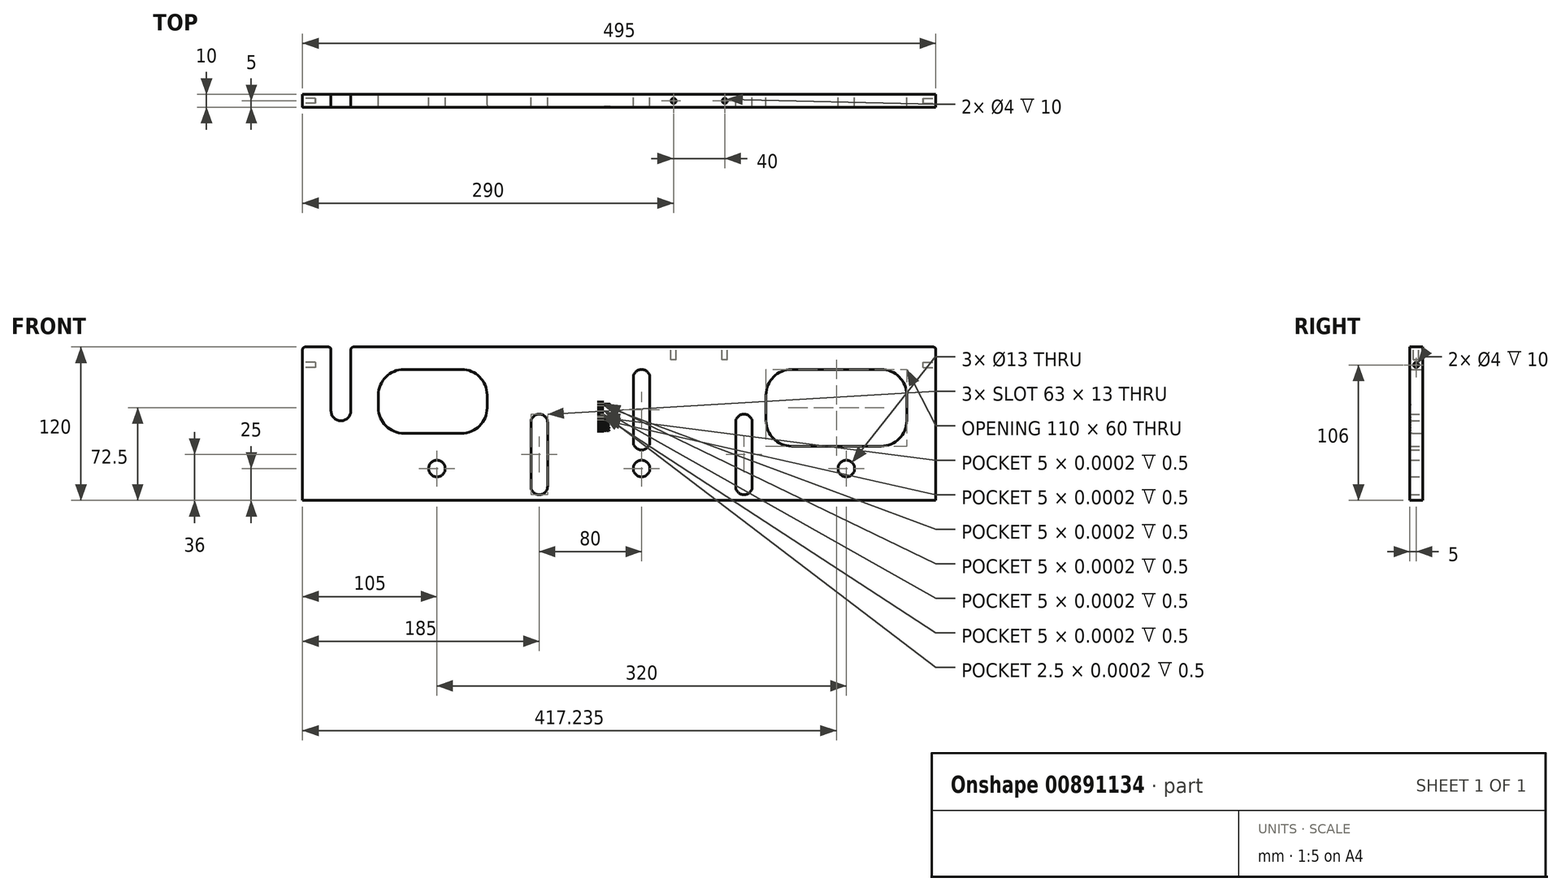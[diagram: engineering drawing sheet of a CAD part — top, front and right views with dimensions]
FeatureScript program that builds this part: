
annotation { "Feature Type Name" : "Feature", "Feature Type Description" : "" }
export const myFeature = defineFeature(function(context is Context, id is Id, definition is map)
    precondition{}
    {
        {
            var Q0;
            Q0=qCreatedBy(makeId("Front.planeOp"),FACE);
            var sketch = newSketch(context, id + "F0", { "sketchPlane" : qUnion([Q0])});
            skLineSegment(sketch, "E0.bottom", {"start": v(-247.5, -60) * mm, "end": v(247.5, -60) * mm});
            skLineSegment(sketch, "E0.top", {"start": v(-247.5, 60) * mm, "end": v(-225.25, 60) * mm});
            skLineSegment(sketch, "E0.left", {"start": v(-247.5, -60) * mm, "end": v(-247.5, 60) * mm});
            skLineSegment(sketch, "E0.right", {"start": v(247.5, -60) * mm, "end": v(247.5, 60) * mm});
            skPoint(sketch, "E0.middle", {"position": v(0, 0) * mm});
            skArc(sketch, "E1", {"start": v(-225.25, 10) * mm, "mid": v(-217.5, 2.25) * mm, "end": v(-209.75, 10) * mm});
            skLineSegment(sketch, "E2", {"start": v(-225.25, 10) * mm, "end": v(-225.25, 60) * mm});
            skLineSegment(sketch, "E3", {"start": v(-209.75, 10) * mm, "end": v(-209.75, 60) * mm});
            skLineSegment(sketch, "E4.trimOffspring", {"start": v(-209.75, 60) * mm, "end": v(247.5, 60) * mm});
            skArc(sketch, "E5", {"start": v(-69, -49) * mm, "mid": v(-62.5, -55.5) * mm, "end": v(-56, -49) * mm});
            skLineSegment(sketch, "E6", {"start": v(17.5, -50) * mm, "end": v(17.5, -10) * mm, "construction": true});
            skLineSegment(sketch, "E7", {"start": v(-62.5, -49) * mm, "end": v(-62.5, 9.6) * mm, "construction": true});
            skLineSegment(sketch, "E8", {"start": v(97.5, -8.77) * mm, "end": v(97.5, -64.84) * mm, "construction": true});
            skArc(sketch, "E9", {"start": v(11, -14) * mm, "mid": v(17.5, -20.5) * mm, "end": v(24, -14) * mm});
            skArc(sketch, "E10", {"start": v(24, 36) * mm, "mid": v(17.5, 42.5) * mm, "end": v(11, 36) * mm});
            skLineSegment(sketch, "E11", {"start": v(11, -14) * mm, "end": v(11, 36) * mm});
            skLineSegment(sketch, "E12.MirrorCS", {"start": v(24, -14) * mm, "end": v(24, 36) * mm});
            skCircle(sketch, "E13", {"center": v(-142.5, -35) * mm, "radius": 6.5 * mm});
            skCircle(sketch, "E14.MirrorC", {"center": v(17.5, -35) * mm, "radius": 6.5 * mm});
            skCircle(sketch, "E15.MirrorC", {"center": v(177.5, -35) * mm, "radius": 6.5 * mm});
            skLineSegment(sketch, "E16", {"start": v(-56, -49) * mm, "end": v(-56, 1) * mm});
            skLineSegment(sketch, "E17.MirrorCS", {"start": v(-69, -49) * mm, "end": v(-69, 1) * mm});
            skArc(sketch, "E18", {"start": v(-56, 1) * mm, "mid": v(-62.5, 7.5) * mm, "end": v(-69, 1) * mm});
            skLineSegment(sketch, "E19.MirrorCS", {"start": v(91, -49) * mm, "end": v(91, 1) * mm});
            skLineSegment(sketch, "E20.MirrorCS", {"start": v(104, -49) * mm, "end": v(104, 1) * mm});
            skArc(sketch, "E21.MirrorCS", {"start": v(91, 1) * mm, "mid": v(97.5, 7.5) * mm, "end": v(104, 1) * mm});
            skPoint(sketch, "E22.orphan", {"position": v(104, -49) * mm});
            skPoint(sketch, "E23.MirrorC.center.orphan", {"position": v(97.5, -49) * mm});
            skPoint(sketch, "E24.MirrorCS.end.orphan", {"position": v(91, -49) * mm});
            skArc(sketch, "E25.MirrorCS", {"start": v(104, -49) * mm, "mid": v(97.5, -55.5) * mm, "end": v(91, -49) * mm});
            skLineSegment(sketch, "E26.bottom", {"start": v(-168.22, 42.5) * mm, "end": v(-123.22, 42.5) * mm});
            skLineSegment(sketch, "E26.top", {"start": v(-168.22, -7.5) * mm, "end": v(-123.22, -7.5) * mm});
            skLineSegment(sketch, "E26.left", {"start": v(-188.22, 22.5) * mm, "end": v(-188.22, 12.5) * mm});
            skLineSegment(sketch, "E26.right", {"start": v(-103.22, 22.5) * mm, "end": v(-103.22, 12.5) * mm});
            skLineSegment(sketch, "E27.bottom", {"start": v(134.73, 42.5) * mm, "end": v(204.73, 42.5) * mm});
            skLineSegment(sketch, "E27.top", {"start": v(134.73, -17.5) * mm, "end": v(204.73, -17.5) * mm});
            skLineSegment(sketch, "E27.left", {"start": v(114.73, 22.5) * mm, "end": v(114.73, 2.5) * mm});
            skLineSegment(sketch, "E27.right", {"start": v(224.73, 22.5) * mm, "end": v(224.73, 2.5) * mm});
            skPoint(sketch, "E28.visualSharp", {"position": v(-188.22, 42.5) * mm});
            skArc(sketch, "E28.filletArc", {"start": v(-168.22, 42.5) * mm, "mid": v(-182.36, 36.64) * mm, "end": v(-188.22, 22.5) * mm});
            skPoint(sketch, "E29.visualSharp", {"position": v(-103.22, 42.5) * mm});
            skArc(sketch, "E29.filletArc", {"start": v(-103.22, 22.5) * mm, "mid": v(-109.08, 36.64) * mm, "end": v(-123.22, 42.5) * mm});
            skPoint(sketch, "E30.visualSharp", {"position": v(-188.22, -7.5) * mm});
            skArc(sketch, "E30.filletArc", {"start": v(-188.22, 12.5) * mm, "mid": v(-182.36, -1.64) * mm, "end": v(-168.22, -7.5) * mm});
            skPoint(sketch, "E31.visualSharp", {"position": v(-103.22, -7.5) * mm});
            skArc(sketch, "E31.filletArc", {"start": v(-123.22, -7.5) * mm, "mid": v(-109.08, -1.64) * mm, "end": v(-103.22, 12.5) * mm});
            skPoint(sketch, "E32.visualSharp", {"position": v(114.73, 42.5) * mm});
            skArc(sketch, "E32.filletArc", {"start": v(134.73, 42.5) * mm, "mid": v(120.6, 36.64) * mm, "end": v(114.73, 22.5) * mm});
            skPoint(sketch, "E33.visualSharp", {"position": v(224.73, -17.5) * mm});
            skArc(sketch, "E33.filletArc", {"start": v(204.73, -17.5) * mm, "mid": v(218.88, -11.64) * mm, "end": v(224.73, 2.5) * mm});
            skPoint(sketch, "E34.visualSharp", {"position": v(224.73, 42.5) * mm});
            skArc(sketch, "E34.filletArc", {"start": v(224.73, 22.5) * mm, "mid": v(218.88, 36.64) * mm, "end": v(204.73, 42.5) * mm});
            skPoint(sketch, "E35.visualSharp", {"position": v(114.73, -17.5) * mm});
            skArc(sketch, "E35.filletArc", {"start": v(114.73, 2.5) * mm, "mid": v(120.6, -11.64) * mm, "end": v(134.73, -17.5) * mm});
            skSolve(sketch);
        }
        {
            var Q0;
            Q0=qSketchRegion(id+"F0",true);
            extrude(context, id + "F1", {"entities" : qUnion([Q0]), "endBound" : BoundingType.SYMMETRIC, "depth" : 10 * mm, "offsetDistance" : 25 * mm});
        }
        {
            var Q0;
            Q0=makeQuery(id+"F1.opExtrude","SWEPT_FACE",FACE,{"disambiguationData":[OSD([sQuery(id+"F0.wireOp",EDGE,"E4.trimOffspring")])]});
            var sketch = newSketch(context, id + "F2", { "sketchPlane" : qUnion([Q0])});
            skLineSegment(sketch, "E36", {"start": v(62.5, 81.53) * mm, "end": v(62.5, -22.42) * mm, "construction": true});
            skCircle(sketch, "E37", {"center": v(42.5, 0) * mm, "radius": 2 * mm});
            skCircle(sketch, "E38.MirrorC", {"center": v(82.5, 0) * mm, "radius": 2 * mm});
            skSolve(sketch);
        }
        {
            var Q0;
            Q0=qSketchRegion(id+"F2",true);
            extrude(context, id + "F3", {"entities" : qUnion([Q0]), "operationType" : NewBodyOperationType.REMOVE, "oppositeDirection" : true, "depth" : 10 * mm, "offsetDistance" : 25 * mm});
        }
        {
            var Q0;
            Q0=makeQuery(id+"F1.opExtrude","SWEPT_EDGE",EDGE,{"disambiguationData":[OSD([sQuery(id+"F0.wireOp",EDGE,"E0.top"),sQuery(id+"F0.wireOp",EDGE,"E2")])]});
            var Q1;
            Q1=makeQuery(id+"F1.opExtrude","SWEPT_EDGE",EDGE,{"disambiguationData":[OSD([sQuery(id+"F0.wireOp",EDGE,"E0.top"),sQuery(id+"F0.wireOp",EDGE,"E0.left")])]});
            var Q2;
            Q2=makeQuery(id+"F1.opExtrude","SWEPT_EDGE",EDGE,{"disambiguationData":[OSD([sQuery(id+"F0.wireOp",EDGE,"E3"),sQuery(id+"F0.wireOp",EDGE,"E4.trimOffspring")])]});
            var Q3;
            Q3=makeQuery(id+"F1.opExtrude","SWEPT_EDGE",EDGE,{"disambiguationData":[OSD([sQuery(id+"F0.wireOp",EDGE,"E0.right"),sQuery(id+"F0.wireOp",EDGE,"E4.trimOffspring")])]});
            fillet(context, id + "F4", {"entities" : qUnion([Q0, Q1, Q2, Q3]), "radius" : 2 * mm, "tangentPropagation" : true, "allowEdgeOverflow" : false});
        }
        {
            var Q0;
            Q0=makeQuery(id+"F1.opExtrude","SWEPT_FACE",FACE,{"disambiguationData":[OSD([sQuery(id+"F0.wireOp",EDGE,"E0.left")])]});
            var sketch = newSketch(context, id + "F5", { "sketchPlane" : qUnion([Q0])});
            skCircle(sketch, "E39", {"center": v(0, 46) * mm, "radius": 2 * mm});
            skSolve(sketch);
        }
        {
            var Q0;
            Q0=makeQuery(id+"F1.opExtrude","SWEPT_FACE",FACE,{"disambiguationData":[OSD([sQuery(id+"F0.wireOp",EDGE,"E0.right")])]});
            var sketch = newSketch(context, id + "F6", { "sketchPlane" : qUnion([Q0])});
            skCircle(sketch, "E40", {"center": v(0, 46) * mm, "radius": 2 * mm});
            skSolve(sketch);
        }
        {
            var Q0;
            Q0 = qSketchRegion(id + "F5", true);
            extrude(context, id + "F7", {"entities" : qUnion([Q0]), "operationType" : NewBodyOperationType.REMOVE, "oppositeDirection" : true, "depth" : 10 * mm, "offsetDistance" : 25 * mm});
        }
        {
            var Q0;
            Q0 = qSketchRegion(id + "F6", true);
            extrude(context, id + "F8", {"entities" : qUnion([Q0]), "operationType" : NewBodyOperationType.REMOVE, "oppositeDirection" : true, "depth" : 10 * mm, "offsetDistance" : 25 * mm});
        }
        {
            var Q0;
            Q0=makeQuery(id+"F1.opExtrude","CAP_FACE",FACE,{"disambiguationData":[OSD([sQuery(id+"F0.wireOp",EDGE,"E0.bottom"),sQuery(id+"F0.wireOp",EDGE,"E0.top"),sQuery(id+"F0.wireOp",EDGE,"E0.left"),sQuery(id+"F0.wireOp",EDGE,"E0.right"),sQuery(id+"F0.wireOp",EDGE,"E1"),sQuery(id+"F0.wireOp",EDGE,"E2"),sQuery(id+"F0.wireOp",EDGE,"E3"),sQuery(id+"F0.wireOp",EDGE,"E4.trimOffspring"),sQuery(id+"F0.wireOp",EDGE,"E5"),sQuery(id+"F0.wireOp",EDGE,"E9"),sQuery(id+"F0.wireOp",EDGE,"E10"),sQuery(id+"F0.wireOp",EDGE,"E11"),sQuery(id+"F0.wireOp",EDGE,"E12.MirrorCS"),sQuery(id+"F0.wireOp",EDGE,"E13"),sQuery(id+"F0.wireOp",EDGE,"E14.MirrorC"),sQuery(id+"F0.wireOp",EDGE,"E15.MirrorC"),sQuery(id+"F0.wireOp",EDGE,"E16"),sQuery(id+"F0.wireOp",EDGE,"E17.MirrorCS"),sQuery(id+"F0.wireOp",EDGE,"E18"),sQuery(id+"F0.wireOp",EDGE,"E19.MirrorCS"),sQuery(id+"F0.wireOp",EDGE,"E20.MirrorCS"),sQuery(id+"F0.wireOp",EDGE,"E21.MirrorCS"),sQuery(id+"F0.wireOp",EDGE,"E25.MirrorCS")])],"isStart":false});
            var sketch = newSketch(context, id + "F9", { "sketchPlane" : qUnion([Q0])});
            skLineSegment(sketch, "E41", {"start": v(17.5, -14) * mm, "end": v(-16.83, -14) * mm, "construction": true});
            skLineSegment(sketch, "E42.bottom", {"start": v(-17, -6) * mm, "end": v(-12, -6) * mm});
            skLineSegment(sketch, "E42.top", {"start": v(-17, -6) * mm, "end": v(-12, -6) * mm});
            skLineSegment(sketch, "E42.left", {"start": v(-17, -6) * mm, "end": v(-17, -6) * mm});
            skLineSegment(sketch, "E42.right", {"start": v(-12, -6) * mm, "end": v(-12, -6) * mm});
            skPoint(sketch, "E42.middle", {"position": v(-14.5, -6) * mm});
            skPoint(sketch, "E43.orphan", {"position": v(-17, -6) * mm});
            skLineSegment(sketch, "E44", {"start": v(-34.94, -5.75) * mm, "end": v(-8.14, -5.75) * mm, "construction": true});
            skLineSegment(sketch, "E45.MirrorCS", {"start": v(-14.5, -5.5) * mm, "end": v(-12, -5.5) * mm});
            skLineSegment(sketch, "E46.MirrorCS", {"start": v(-12, -5.5) * mm, "end": v(-12, -5.5) * mm});
            skLineSegment(sketch, "E47", {"start": v(-17, -5.3) * mm, "end": v(-16.3, -5.3) * mm, "construction": true});
            skLineSegment(sketch, "E48", {"start": v(-17, -5.5) * mm, "end": v(-16.28, -5.5) * mm, "construction": true});
            skLineSegment(sketch, "E49", {"start": v(-17, -6) * mm, "end": v(-16.85, -6) * mm, "construction": true});
            skLineSegment(sketch, "E50", {"start": v(-14.5, -5.5) * mm, "end": v(-14.5, -5.5) * mm});
            skLineSegment(sketch, "E51.MirrorCS", {"start": v(-17, -5) * mm, "end": v(-12, -5) * mm});
            skLineSegment(sketch, "E52.MirrorCS", {"start": v(-17, -5) * mm, "end": v(-17, -5) * mm});
            skLineSegment(sketch, "E53.MirrorCS", {"start": v(-17, -5) * mm, "end": v(-16.85, -5) * mm, "construction": true});
            skLineSegment(sketch, "E54.MirrorCS", {"start": v(-12, -5) * mm, "end": v(-12, -5) * mm});
            skLineSegment(sketch, "E55.MirrorCS", {"start": v(-17, -4) * mm, "end": v(-12, -4) * mm});
            skLineSegment(sketch, "E56.MirrorCS", {"start": v(-17, -4) * mm, "end": v(-17, -4) * mm});
            skLineSegment(sketch, "E57.MirrorCS", {"start": v(-12, -4) * mm, "end": v(-12, -4) * mm});
            skLineSegment(sketch, "E58.MirrorCS", {"start": v(-17, -4) * mm, "end": v(-16.85, -4) * mm, "construction": true});
            skLineSegment(sketch, "E59.MirrorCS", {"start": v(-14.5, -4.5) * mm, "end": v(-12, -4.5) * mm});
            skLineSegment(sketch, "E60.MirrorCS", {"start": v(-14.5, -4.5) * mm, "end": v(-14.5, -4.5) * mm});
            skLineSegment(sketch, "E61.MirrorCS", {"start": v(-12, -4.5) * mm, "end": v(-12, -4.5) * mm});
            skLineSegment(sketch, "E62.MirrorCS", {"start": v(-14.5, -3.5) * mm, "end": v(-12, -3.5) * mm});
            skLineSegment(sketch, "E63.MirrorCS", {"start": v(-14.5, -3.5) * mm, "end": v(-14.5, -3.5) * mm});
            skLineSegment(sketch, "E64.MirrorCS", {"start": v(-12, -3.5) * mm, "end": v(-12, -3.5) * mm});
            skLineSegment(sketch, "E65", {"start": v(-14.58, -3.5) * mm, "end": v(-14.5, -3.5) * mm, "construction": true});
            skLineSegment(sketch, "E66.MirrorCS", {"start": v(-12, -2) * mm, "end": v(-12, -2) * mm});
            skLineSegment(sketch, "E67.MirrorCS", {"start": v(-17, -2) * mm, "end": v(-16.85, -2) * mm, "construction": true});
            skLineSegment(sketch, "E68.MirrorCS", {"start": v(-17, -1) * mm, "end": v(-16.85, -1) * mm, "construction": true});
            skLineSegment(sketch, "E69.MirrorCS", {"start": v(-17, -1) * mm, "end": v(-17, -1) * mm});
            skLineSegment(sketch, "E70.MirrorCS", {"start": v(-17, -2) * mm, "end": v(-17, -2) * mm});
            skLineSegment(sketch, "E71.MirrorCS", {"start": v(-17, -3) * mm, "end": v(-16.85, -3) * mm, "construction": true});
            skLineSegment(sketch, "E72.MirrorCS", {"start": v(-12, -1.5) * mm, "end": v(-12, -1.5) * mm});
            skLineSegment(sketch, "E73.MirrorCS", {"start": v(-12, -1) * mm, "end": v(-12, -1) * mm});
            skLineSegment(sketch, "E74.MirrorCS", {"start": v(-12, -2.5) * mm, "end": v(-12, -2.5) * mm});
            skLineSegment(sketch, "E75.MirrorCS", {"start": v(-12, -3) * mm, "end": v(-12, -3) * mm});
            skLineSegment(sketch, "E76.MirrorCS", {"start": v(-14.5, -1.5) * mm, "end": v(-14.5, -1.5) * mm});
            skLineSegment(sketch, "E77.MirrorCS", {"start": v(-17, -3) * mm, "end": v(-17, -3) * mm});
            skLineSegment(sketch, "E78.MirrorCS", {"start": v(-14.5, -2.5) * mm, "end": v(-14.5, -2.5) * mm});
            skLineSegment(sketch, "E79.MirrorCS", {"start": v(-14.5, -1.5) * mm, "end": v(-12, -1.5) * mm});
            skLineSegment(sketch, "E80.MirrorCS", {"start": v(-17, -2) * mm, "end": v(-12, -2) * mm});
            skLineSegment(sketch, "E81.MirrorCS", {"start": v(-17, -1.5) * mm, "end": v(-16.28, -1.5) * mm, "construction": true});
            skLineSegment(sketch, "E82.MirrorCS", {"start": v(-17, -1.7) * mm, "end": v(-16.3, -1.7) * mm, "construction": true});
            skLineSegment(sketch, "E83.MirrorCS", {"start": v(-17, -1) * mm, "end": v(-12, -1) * mm});
            skLineSegment(sketch, "E84.MirrorCS", {"start": v(-14.5, -2.5) * mm, "end": v(-12, -2.5) * mm});
            skLineSegment(sketch, "E85.MirrorCS", {"start": v(-17, -3) * mm, "end": v(-12, -3) * mm});
            skPoint(sketch, "E86.MirrorP", {"position": v(-17, -1) * mm});
            skPoint(sketch, "E87.MirrorP", {"position": v(-14.5, -1) * mm});
            skLineSegment(sketch, "E88.MirrorCS", {"start": v(-14.5, -0.5) * mm, "end": v(-14.5, -0.5) * mm});
            skLineSegment(sketch, "E89.MirrorCS", {"start": v(-14.5, -0.5) * mm, "end": v(-12, -0.5) * mm});
            skLineSegment(sketch, "E90.MirrorCS", {"start": v(-12, -0.5) * mm, "end": v(-12, -0.5) * mm});
            skLineSegment(sketch, "E91", {"start": v(-14.72, -0.5) * mm, "end": v(-14.5, -0.5) * mm, "construction": true});
            skLineSegment(sketch, "E92", {"start": v(-32.7, -1.5) * mm, "end": v(-14.5, -1.5) * mm, "construction": true});
            skLineSegment(sketch, "E93.MirrorCS", {"start": v(-12, 1.5) * mm, "end": v(-12, 1.5) * mm});
            skLineSegment(sketch, "E94.MirrorCS", {"start": v(-17, 0) * mm, "end": v(-16.85, 0) * mm, "construction": true});
            skLineSegment(sketch, "E95.MirrorCS", {"start": v(-17, 0) * mm, "end": v(-17, 0) * mm});
            skLineSegment(sketch, "E96.MirrorCS", {"start": v(-17, 4) * mm, "end": v(-17, 4) * mm});
            skLineSegment(sketch, "E97.MirrorCS", {"start": v(-12, 4) * mm, "end": v(-12, 4) * mm});
            skLineSegment(sketch, "E98.MirrorCS", {"start": v(-17, 4) * mm, "end": v(-16.85, 4) * mm, "construction": true});
            skLineSegment(sketch, "E99.MirrorCS", {"start": v(-14.5, 1.5) * mm, "end": v(-14.5, 1.5) * mm});
            skLineSegment(sketch, "E100.MirrorCS", {"start": v(-17, 5) * mm, "end": v(-16.85, 5) * mm, "construction": true});
            skLineSegment(sketch, "E101.MirrorCS", {"start": v(-17, 5) * mm, "end": v(-17, 5) * mm});
            skLineSegment(sketch, "E102.MirrorCS", {"start": v(-12, 1) * mm, "end": v(-12, 1) * mm});
            skLineSegment(sketch, "E103.MirrorCS", {"start": v(-12, 2.5) * mm, "end": v(-12, 2.5) * mm});
            skLineSegment(sketch, "E104.MirrorCS", {"start": v(-12, 3.5) * mm, "end": v(-12, 3.5) * mm});
            skLineSegment(sketch, "E105.MirrorCS", {"start": v(-14.5, 2.5) * mm, "end": v(-14.5, 2.5) * mm});
            skLineSegment(sketch, "E106.MirrorCS", {"start": v(-12, 0) * mm, "end": v(-12, 0) * mm});
            skLineSegment(sketch, "E107.MirrorCS", {"start": v(-14.58, 2.5) * mm, "end": v(-14.5, 2.5) * mm, "construction": true});
            skLineSegment(sketch, "E108.MirrorCS", {"start": v(-17, 1) * mm, "end": v(-17, 1) * mm});
            skLineSegment(sketch, "E109.MirrorCS", {"start": v(-12, 5) * mm, "end": v(-12, 5) * mm});
            skLineSegment(sketch, "E110.MirrorCS", {"start": v(-17, 1) * mm, "end": v(-16.85, 1) * mm, "construction": true});
            skLineSegment(sketch, "E111.MirrorCS", {"start": v(-12, 2) * mm, "end": v(-12, 2) * mm});
            skLineSegment(sketch, "E112.MirrorCS", {"start": v(-32.7, 0.5) * mm, "end": v(-14.5, 0.5) * mm, "construction": true});
            skLineSegment(sketch, "E113.MirrorCS", {"start": v(-17, 2) * mm, "end": v(-16.85, 2) * mm, "construction": true});
            skLineSegment(sketch, "E114.MirrorCS", {"start": v(-17, 3) * mm, "end": v(-17, 3) * mm});
            skLineSegment(sketch, "E115.MirrorCS", {"start": v(-14.5, 0.5) * mm, "end": v(-14.5, 0.5) * mm});
            skLineSegment(sketch, "E116.MirrorCS", {"start": v(-12, 0.5) * mm, "end": v(-12, 0.5) * mm});
            skLineSegment(sketch, "E117.MirrorCS", {"start": v(-12, 3) * mm, "end": v(-12, 3) * mm});
            skLineSegment(sketch, "E118.MirrorCS", {"start": v(-17, 3) * mm, "end": v(-16.85, 3) * mm, "construction": true});
            skLineSegment(sketch, "E119.MirrorCS", {"start": v(-17, 2) * mm, "end": v(-17, 2) * mm});
            skLineSegment(sketch, "E120.MirrorCS", {"start": v(-14.5, 4.5) * mm, "end": v(-14.5, 4.5) * mm});
            skLineSegment(sketch, "E121.MirrorCS", {"start": v(-14.5, 3.5) * mm, "end": v(-14.5, 3.5) * mm});
            skLineSegment(sketch, "E122.MirrorCS", {"start": v(-12, 4.5) * mm, "end": v(-12, 4.5) * mm});
            skLineSegment(sketch, "E123.MirrorCS", {"start": v(-17, 0.5) * mm, "end": v(-16.28, 0.5) * mm, "construction": true});
            skLineSegment(sketch, "E124.MirrorCS", {"start": v(-17, 0.7) * mm, "end": v(-16.3, 0.7) * mm, "construction": true});
            skLineSegment(sketch, "E125.MirrorCS", {"start": v(-14.5, 2.5) * mm, "end": v(-12, 2.5) * mm});
            skPoint(sketch, "E126.MirrorP", {"position": v(-17, 0) * mm});
            skLineSegment(sketch, "E127.MirrorCS", {"start": v(-17, 4.5) * mm, "end": v(-16.28, 4.5) * mm, "construction": true});
            skLineSegment(sketch, "E128.MirrorCS", {"start": v(-17, 4) * mm, "end": v(-12, 4) * mm});
            skLineSegment(sketch, "E129.MirrorCS", {"start": v(-14.5, 1.5) * mm, "end": v(-12, 1.5) * mm});
            skLineSegment(sketch, "E130.MirrorCS", {"start": v(-17, 4.3) * mm, "end": v(-16.3, 4.3) * mm, "construction": true});
            skLineSegment(sketch, "E131.MirrorCS", {"start": v(-17, 0) * mm, "end": v(-12, 0) * mm});
            skLineSegment(sketch, "E132.MirrorCS", {"start": v(-17, 2) * mm, "end": v(-12, 2) * mm});
            skLineSegment(sketch, "E133.MirrorCS", {"start": v(-17, 3) * mm, "end": v(-12, 3) * mm});
            skLineSegment(sketch, "E134.MirrorCS", {"start": v(-17, 1) * mm, "end": v(-12, 1) * mm});
            skLineSegment(sketch, "E135.MirrorCS", {"start": v(-17, 5) * mm, "end": v(-12, 5) * mm});
            skPoint(sketch, "E136.MirrorP", {"position": v(-14.5, 5) * mm});
            skLineSegment(sketch, "E137.MirrorCS", {"start": v(-14.5, 3.5) * mm, "end": v(-12, 3.5) * mm});
            skLineSegment(sketch, "E138.MirrorCS", {"start": v(-14.5, 4.5) * mm, "end": v(-12, 4.5) * mm});
            skLineSegment(sketch, "E139.MirrorCS", {"start": v(-14.5, 0.5) * mm, "end": v(-12, 0.5) * mm});
            skPoint(sketch, "E140.MirrorP", {"position": v(-14.5, 0) * mm});
            skPoint(sketch, "E141.MirrorP", {"position": v(-17, 5) * mm});
            skLineSegment(sketch, "E142.MirrorCS", {"start": v(-14.5, 5.5) * mm, "end": v(-12, 5.5) * mm});
            skLineSegment(sketch, "E143.MirrorCS", {"start": v(-14.5, 5.5) * mm, "end": v(-14.5, 5.5) * mm});
            skLineSegment(sketch, "E144.MirrorCS", {"start": v(-12, 5.5) * mm, "end": v(-12, 5.5) * mm});
            skLineSegment(sketch, "E145", {"start": v(-14.5, 5.5) * mm, "end": v(-14.36, 5.5) * mm, "construction": true});
            skLineSegment(sketch, "E146.MirrorCS", {"start": v(-12, 6.5) * mm, "end": v(-12, 6.5) * mm});
            skLineSegment(sketch, "E147.MirrorCS", {"start": v(-12, 7) * mm, "end": v(-12, 7) * mm});
            skLineSegment(sketch, "E148.MirrorCS", {"start": v(-12, 7.5) * mm, "end": v(-12, 7.5) * mm});
            skLineSegment(sketch, "E149.MirrorCS", {"start": v(-17, 14) * mm, "end": v(-16.85, 14) * mm, "construction": true});
            skLineSegment(sketch, "E150.MirrorCS", {"start": v(-17, 16) * mm, "end": v(-17, 16) * mm});
            skLineSegment(sketch, "E151.MirrorCS", {"start": v(-17, 7) * mm, "end": v(-17, 7) * mm});
            skLineSegment(sketch, "E152.MirrorCS", {"start": v(-12, 9) * mm, "end": v(-12, 9) * mm});
            skLineSegment(sketch, "E153.MirrorCS", {"start": v(-14.5, 11.5) * mm, "end": v(-14.5, 11.5) * mm});
            skLineSegment(sketch, "E154.MirrorCS", {"start": v(-17, 9) * mm, "end": v(-17, 9) * mm});
            skLineSegment(sketch, "E155.MirrorCS", {"start": v(-17, 9) * mm, "end": v(-16.85, 9) * mm, "construction": true});
            skLineSegment(sketch, "E156.MirrorCS", {"start": v(-17, 14) * mm, "end": v(-17, 14) * mm});
            skLineSegment(sketch, "E157.MirrorCS", {"start": v(-14.72, 11.5) * mm, "end": v(-14.5, 11.5) * mm, "construction": true});
            skLineSegment(sketch, "E158.MirrorCS", {"start": v(-12, 10) * mm, "end": v(-12, 10) * mm});
            skLineSegment(sketch, "E159.MirrorCS", {"start": v(-12, 15.5) * mm, "end": v(-12, 15.5) * mm});
            skLineSegment(sketch, "E160.MirrorCS", {"start": v(-17, 11) * mm, "end": v(-17, 11) * mm});
            skLineSegment(sketch, "E161.MirrorCS", {"start": v(-17, 6) * mm, "end": v(-17, 6) * mm});
            skLineSegment(sketch, "E162.MirrorCS", {"start": v(-14.5, 6.5) * mm, "end": v(-14.5, 6.5) * mm});
            skLineSegment(sketch, "E163.MirrorCS", {"start": v(-12, 8.5) * mm, "end": v(-12, 8.5) * mm});
            skLineSegment(sketch, "E164.MirrorCS", {"start": v(-17, 6) * mm, "end": v(-16.85, 6) * mm, "construction": true});
            skLineSegment(sketch, "E165.MirrorCS", {"start": v(-17, 10) * mm, "end": v(-17, 10) * mm});
            skLineSegment(sketch, "E166.MirrorCS", {"start": v(-17, 16) * mm, "end": v(-16.85, 16) * mm, "construction": true});
            skLineSegment(sketch, "E167.MirrorCS", {"start": v(-12, 14) * mm, "end": v(-12, 14) * mm});
            skLineSegment(sketch, "E168.MirrorCS", {"start": v(-12, 11.5) * mm, "end": v(-12, 11.5) * mm});
            skLineSegment(sketch, "E169.MirrorCS", {"start": v(-14.5, 15.5) * mm, "end": v(-14.5, 15.5) * mm});
            skLineSegment(sketch, "E170.MirrorCS", {"start": v(-12, 10.5) * mm, "end": v(-12, 10.5) * mm});
            skLineSegment(sketch, "E171.MirrorCS", {"start": v(-12, 15) * mm, "end": v(-12, 15) * mm});
            skLineSegment(sketch, "E172.MirrorCS", {"start": v(-14.5, 7.5) * mm, "end": v(-14.5, 7.5) * mm});
            skLineSegment(sketch, "E173.MirrorCS", {"start": v(-17, 7) * mm, "end": v(-16.85, 7) * mm, "construction": true});
            skLineSegment(sketch, "E174.MirrorCS", {"start": v(-12, 8) * mm, "end": v(-12, 8) * mm});
            skLineSegment(sketch, "E175.MirrorCS", {"start": v(-12, 14.5) * mm, "end": v(-12, 14.5) * mm});
            skLineSegment(sketch, "E176.MirrorCS", {"start": v(-12, 6) * mm, "end": v(-12, 6) * mm});
            skLineSegment(sketch, "E177.MirrorCS", {"start": v(-12, 13.5) * mm, "end": v(-12, 13.5) * mm});
            skLineSegment(sketch, "E178.MirrorCS", {"start": v(-17, 10) * mm, "end": v(-16.85, 10) * mm, "construction": true});
            skLineSegment(sketch, "E179.MirrorCS", {"start": v(-17, 12) * mm, "end": v(-17, 12) * mm});
            skLineSegment(sketch, "E180.MirrorCS", {"start": v(-17, 11) * mm, "end": v(-16.85, 11) * mm, "construction": true});
            skLineSegment(sketch, "E181.MirrorCS", {"start": v(-17, 15) * mm, "end": v(-16.85, 15) * mm, "construction": true});
            skLineSegment(sketch, "E182.MirrorCS", {"start": v(-32.7, 10.5) * mm, "end": v(-14.5, 10.5) * mm, "construction": true});
            skLineSegment(sketch, "E183.MirrorCS", {"start": v(-17, 8) * mm, "end": v(-16.85, 8) * mm, "construction": true});
            skLineSegment(sketch, "E184.MirrorCS", {"start": v(-17, 8) * mm, "end": v(-17, 8) * mm});
            skLineSegment(sketch, "E185.MirrorCS", {"start": v(-14.5, 10.5) * mm, "end": v(-14.5, 10.5) * mm});
            skLineSegment(sketch, "E186.MirrorCS", {"start": v(-12, 16.5) * mm, "end": v(-12, 16.5) * mm});
            skLineSegment(sketch, "E187.MirrorCS", {"start": v(-12, 12.5) * mm, "end": v(-12, 12.5) * mm});
            skLineSegment(sketch, "E188.MirrorCS", {"start": v(-17, 12) * mm, "end": v(-16.85, 12) * mm, "construction": true});
            skLineSegment(sketch, "E189.MirrorCS", {"start": v(-17, 17) * mm, "end": v(-17, 17) * mm});
            skLineSegment(sketch, "E190.MirrorCS", {"start": v(-12, 16) * mm, "end": v(-12, 16) * mm});
            skLineSegment(sketch, "E191.MirrorCS", {"start": v(-14.5, 8.5) * mm, "end": v(-14.5, 8.5) * mm});
            skLineSegment(sketch, "E192.MirrorCS", {"start": v(-14.58, 14.5) * mm, "end": v(-14.5, 14.5) * mm, "construction": true});
            skLineSegment(sketch, "E193.MirrorCS", {"start": v(-12, 17) * mm, "end": v(-12, 17) * mm});
            skLineSegment(sketch, "E194.MirrorCS", {"start": v(-14.58, 8.5) * mm, "end": v(-14.5, 8.5) * mm, "construction": true});
            skLineSegment(sketch, "E195.MirrorCS", {"start": v(-12, 13) * mm, "end": v(-12, 13) * mm});
            skLineSegment(sketch, "E196.MirrorCS", {"start": v(-17, 13) * mm, "end": v(-17, 13) * mm});
            skLineSegment(sketch, "E197.MirrorCS", {"start": v(-12, 11) * mm, "end": v(-12, 11) * mm});
            skLineSegment(sketch, "E198.MirrorCS", {"start": v(-17, 13) * mm, "end": v(-16.85, 13) * mm, "construction": true});
            skLineSegment(sketch, "E199.MirrorCS", {"start": v(-12, 9.5) * mm, "end": v(-12, 9.5) * mm});
            skLineSegment(sketch, "E200.MirrorCS", {"start": v(-17, 17) * mm, "end": v(-16.85, 17) * mm, "construction": true});
            skLineSegment(sketch, "E201.MirrorCS", {"start": v(-17, 15) * mm, "end": v(-17, 15) * mm});
            skLineSegment(sketch, "E202.MirrorCS", {"start": v(-32.7, 12.5) * mm, "end": v(-14.5, 12.5) * mm, "construction": true});
            skLineSegment(sketch, "E203.MirrorCS", {"start": v(-12, 12) * mm, "end": v(-12, 12) * mm});
            skLineSegment(sketch, "E204.MirrorCS", {"start": v(-14.5, 14.5) * mm, "end": v(-14.5, 14.5) * mm});
            skLineSegment(sketch, "E205.MirrorCS", {"start": v(-14.5, 12.5) * mm, "end": v(-14.5, 12.5) * mm});
            skLineSegment(sketch, "E206.MirrorCS", {"start": v(-14.5, 16.5) * mm, "end": v(-14.5, 16.5) * mm});
            skLineSegment(sketch, "E207.MirrorCS", {"start": v(-14.5, 13.5) * mm, "end": v(-14.5, 13.5) * mm});
            skLineSegment(sketch, "E208.MirrorCS", {"start": v(-14.5, 9.5) * mm, "end": v(-14.5, 9.5) * mm});
            skLineSegment(sketch, "E209.MirrorCS", {"start": v(-17, 12.5) * mm, "end": v(-16.28, 12.5) * mm, "construction": true});
            skLineSegment(sketch, "E210.MirrorCS", {"start": v(-17, 14) * mm, "end": v(-12, 14) * mm});
            skPoint(sketch, "E211.MirrorP", {"position": v(-17, 6) * mm});
            skLineSegment(sketch, "E212.MirrorCS", {"start": v(-17, 17) * mm, "end": v(-12, 17) * mm});
            skLineSegment(sketch, "E213.MirrorCS", {"start": v(-17, 10.3) * mm, "end": v(-16.3, 10.3) * mm, "construction": true});
            skLineSegment(sketch, "E214.MirrorCS", {"start": v(-17, 12.7) * mm, "end": v(-16.3, 12.7) * mm, "construction": true});
            skLineSegment(sketch, "E215.MirrorCS", {"start": v(-14.5, 11.5) * mm, "end": v(-12, 11.5) * mm});
            skLineSegment(sketch, "E216.MirrorCS", {"start": v(-14.5, 8.5) * mm, "end": v(-12, 8.5) * mm});
            skLineSegment(sketch, "E217.MirrorCS", {"start": v(-14.5, 15.5) * mm, "end": v(-12, 15.5) * mm});
            skLineSegment(sketch, "E218.MirrorCS", {"start": v(-17, 6.7) * mm, "end": v(-16.3, 6.7) * mm, "construction": true});
            skLineSegment(sketch, "E219.MirrorCS", {"start": v(-17, 6.5) * mm, "end": v(-16.28, 6.5) * mm, "construction": true});
            skLineSegment(sketch, "E220.MirrorCS", {"start": v(-17, 16.5) * mm, "end": v(-16.28, 16.5) * mm, "construction": true});
            skLineSegment(sketch, "E221.MirrorCS", {"start": v(-17, 16.3) * mm, "end": v(-16.3, 16.3) * mm, "construction": true});
            skPoint(sketch, "E222.MirrorP", {"position": v(-17, 17) * mm});
            skLineSegment(sketch, "E223.MirrorCS", {"start": v(-14.5, 6.5) * mm, "end": v(-12, 6.5) * mm});
            skLineSegment(sketch, "E224.MirrorCS", {"start": v(-17, 10.5) * mm, "end": v(-16.28, 10.5) * mm, "construction": true});
            skLineSegment(sketch, "E225.MirrorCS", {"start": v(-14.5, 14.5) * mm, "end": v(-12, 14.5) * mm});
            skLineSegment(sketch, "E226.MirrorCS", {"start": v(-14.5, 7.5) * mm, "end": v(-12, 7.5) * mm});
            skLineSegment(sketch, "E227.MirrorCS", {"start": v(-17, 9) * mm, "end": v(-12, 9) * mm});
            skLineSegment(sketch, "E228.MirrorCS", {"start": v(-14.5, 9.5) * mm, "end": v(-12, 9.5) * mm});
            skLineSegment(sketch, "E229.MirrorCS", {"start": v(-14.5, 13.5) * mm, "end": v(-12, 13.5) * mm});
            skLineSegment(sketch, "E230.MirrorCS", {"start": v(-14.5, 16.5) * mm, "end": v(-12, 16.5) * mm});
            skLineSegment(sketch, "E231.MirrorCS", {"start": v(-14.5, 10.5) * mm, "end": v(-12, 10.5) * mm});
            skLineSegment(sketch, "E232.MirrorCS", {"start": v(-14.5, 12.5) * mm, "end": v(-12, 12.5) * mm});
            skLineSegment(sketch, "E233.MirrorCS", {"start": v(-17, 13) * mm, "end": v(-12, 13) * mm});
            skPoint(sketch, "E234.MirrorP", {"position": v(-14.5, 6) * mm});
            skLineSegment(sketch, "E235.MirrorCS", {"start": v(-17, 8) * mm, "end": v(-12, 8) * mm});
            skPoint(sketch, "E236.MirrorP", {"position": v(-17, 11) * mm});
            skLineSegment(sketch, "E237.MirrorCS", {"start": v(-17, 6) * mm, "end": v(-12, 6) * mm});
            skLineSegment(sketch, "E238.MirrorCS", {"start": v(-17, 15) * mm, "end": v(-12, 15) * mm});
            skLineSegment(sketch, "E239.MirrorCS", {"start": v(-17, 7) * mm, "end": v(-12, 7) * mm});
            skPoint(sketch, "E240.MirrorP", {"position": v(-17, 12) * mm});
            skPoint(sketch, "E241.MirrorP", {"position": v(-14.5, 17) * mm});
            skLineSegment(sketch, "E242.MirrorCS", {"start": v(-34.94, 16.75) * mm, "end": v(-8.14, 16.75) * mm, "construction": true});
            skPoint(sketch, "E243.MirrorP", {"position": v(-14.5, 11) * mm});
            skLineSegment(sketch, "E244.MirrorCS", {"start": v(-17, 12) * mm, "end": v(-12, 12) * mm});
            skLineSegment(sketch, "E245.MirrorCS", {"start": v(-17, 10) * mm, "end": v(-12, 10) * mm});
            skLineSegment(sketch, "E246.MirrorCS", {"start": v(-17, 11) * mm, "end": v(-12, 11) * mm});
            skLineSegment(sketch, "E247.MirrorCS", {"start": v(-17, 16) * mm, "end": v(-12, 16) * mm});
            skPoint(sketch, "E248.MirrorP", {"position": v(-14.5, 12) * mm});
            skLineSegment(sketch, "E249", {"start": v(-11.95, -6.24) * mm, "end": v(-11.63, -6.24) * mm, "construction": true});
            skLineSegment(sketch, "E250.MirrorCS", {"start": v(-34.94, -6.25) * mm, "end": v(-8.14, -6.25) * mm, "construction": true});
            skText(sketch, "E251", { "text": " 0 mm", "fontName": "OpenSans-Regular.ttf"});
            skText(sketch, "E252", { "text": " 2 mm", "fontName": "OpenSans-Regular.ttf"});
            skText(sketch, "E253", { "text": " 4 mm", "fontName": "OpenSans-Regular.ttf"});
            skText(sketch, "E254", { "text": " 6 mm", "fontName": "OpenSans-Regular.ttf"});
            skText(sketch, "E255", { "text": " 8 mm", "fontName": "OpenSans-Regular.ttf"});
            skText(sketch, "E256", { "text": " 10 mm", "fontName": "OpenSans-Regular.ttf"});
            skText(sketch, "E257", { "text": " 20 mm", "fontName": "OpenSans-Regular.ttf"});
            const initialGuessF9  = {"E251": [-0.012, -0.0055, 1, 0, 0.001], "E252": [-0.012, -0.00355, 1, 0, 0.00105], "E253": [-0.012, -0.00142, 1, 0, 0.00093], "E254": [-0.012, 0.00048, 1, 0, 0.00102], "E255": [-0.01185, 0.0025, 1, 0, 0.001], "E256": [-0.01185, 0.0045, 1, 0, 0.001], "E257": [-0.0118, 0.01451, 1, 0, 0.001]};
            skSetInitialGuess(sketch, initialGuessF9);
            skSolve(sketch);
        }
        {
            var Q0;
            Q0 = qSketchRegion(id + "F9", true);
            extrude(context, id + "F10", {"entities" : qUnion([Q0]), "operationType" : NewBodyOperationType.REMOVE, "oppositeDirection" : true, "depth" : 0.5 * mm, "offsetDistance" : 25 * mm});
        }
        {
            var Q0;
            Q0=makeQuery(id+"F1.opExtrude","CAP_EDGE",EDGE,{"disambiguationData":[OSD([sQuery(id+"F0.wireOp",EDGE,"E26.top")])],"isStart":false});
            var Q1;
            Q1=makeQuery(id+"F1.opExtrude","CAP_EDGE",EDGE,{"disambiguationData":[OSD([sQuery(id+"F0.wireOp",EDGE,"E28.filletArc")])],"isStart":false});
            var Q2;
            Q2=makeQuery(id+"F1.opExtrude","CAP_EDGE",EDGE,{"disambiguationData":[OSD([sQuery(id+"F0.wireOp",EDGE,"E30.filletArc")])],"isStart":false});
            var Q3;
            Q3=makeQuery(id+"F1.opExtrude","CAP_EDGE",EDGE,{"disambiguationData":[OSD([sQuery(id+"F0.wireOp",EDGE,"E26.left")])],"isStart":false});
            var Q4;
            Q4=makeQuery(id+"F1.opExtrude","CAP_EDGE",EDGE,{"disambiguationData":[OSD([sQuery(id+"F0.wireOp",EDGE,"E26.bottom")])],"isStart":false});
            var Q5;
            Q5=makeQuery(id+"F1.opExtrude","CAP_EDGE",EDGE,{"disambiguationData":[OSD([sQuery(id+"F0.wireOp",EDGE,"E29.filletArc")])],"isStart":false});
            var Q6;
            Q6=makeQuery(id+"F1.opExtrude","CAP_EDGE",EDGE,{"disambiguationData":[OSD([sQuery(id+"F0.wireOp",EDGE,"E26.right")])],"isStart":false});
            var Q7;
            Q7=makeQuery(id+"F1.opExtrude","CAP_EDGE",EDGE,{"disambiguationData":[OSD([sQuery(id+"F0.wireOp",EDGE,"E31.filletArc")])],"isStart":false});
            fillet(context, id + "F11", {"entities" : qUnion([Q0, Q1, Q2, Q3, Q4, Q5, Q6, Q7]), "radius" : 2 * mm, "tangentPropagation" : true, "allowEdgeOverflow" : false});
        }
    });
